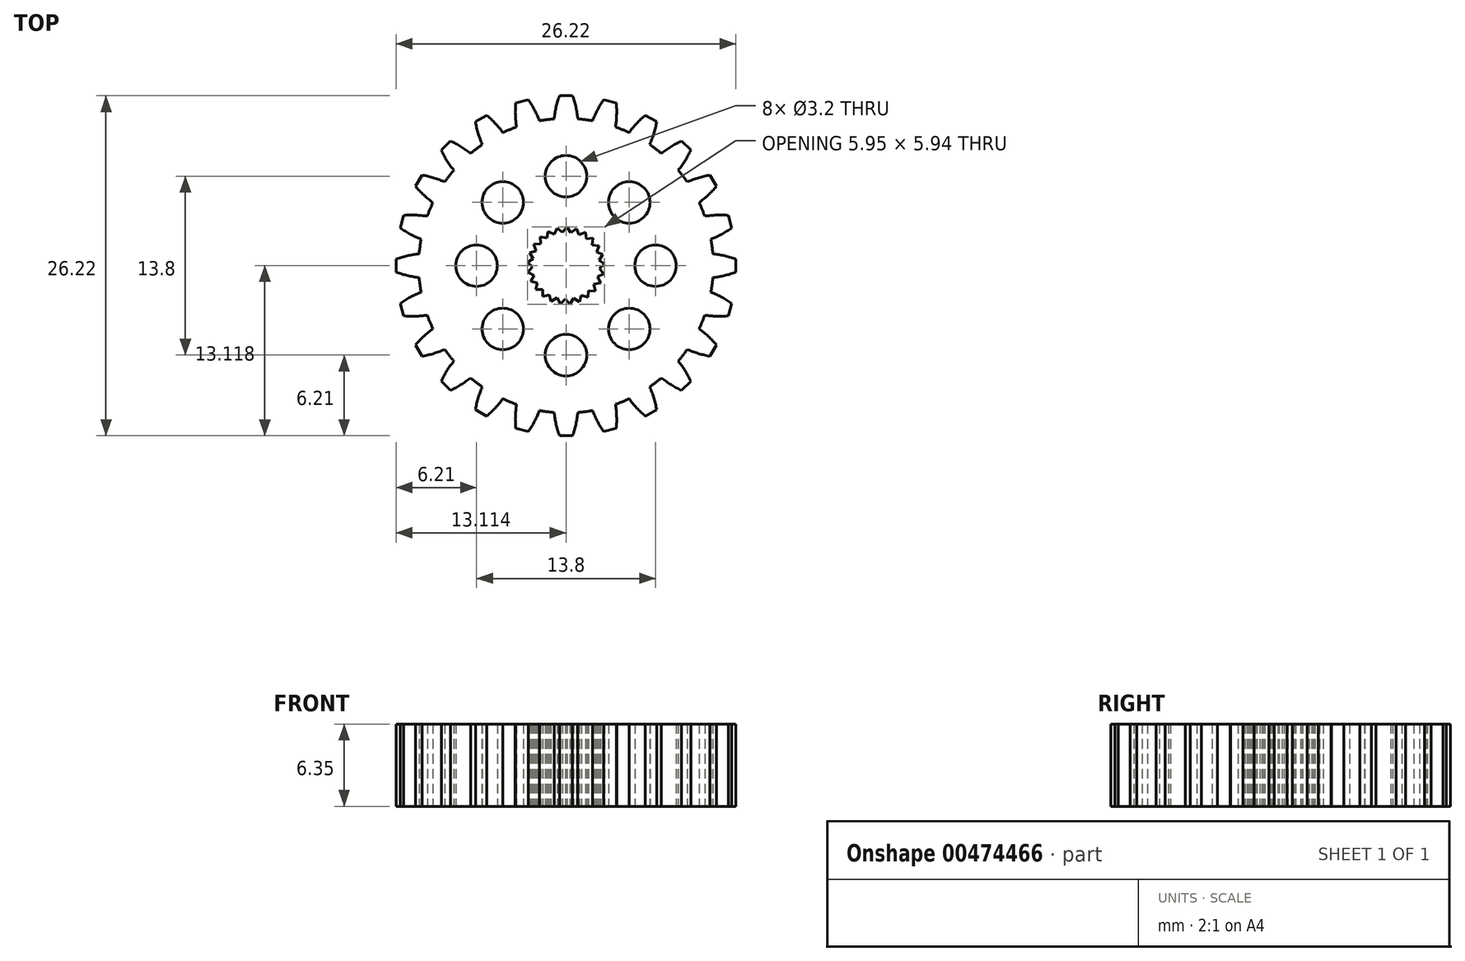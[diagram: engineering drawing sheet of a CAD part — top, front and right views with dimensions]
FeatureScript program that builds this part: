
annotation { "Feature Type Name" : "Feature", "Feature Type Description" : "" }
export const myFeature = defineFeature(function(context is Context, id is Id, definition is map)
    precondition{}
    {
        {
            var Q0;
            Q0=qCreatedBy(makeId("Top.planeOp"),FACE);
            var sketch = newSketch(context, id + "F0", { "sketchPlane" : qUnion([Q0])});
            skLineSegment(sketch, "E0", {"start": v(-0.5, 13.1) * mm, "end": v(0.5, 13.1) * mm});
            skArc(sketch, "E1", {"start": v(-0.5, 13.1) * mm, "mid": v(-0.76, 12.23) * mm, "end": v(-0.91, 11.32) * mm});
            skArc(sketch, "E2.MirrorCS", {"start": v(0.5, 13.1) * mm, "mid": v(0.76, 12.23) * mm, "end": v(0.91, 11.32) * mm});
            skPoint(sketch, "E3.center", {"position": v(0, 0) * mm});
            skLineSegment(sketch, "E4", {"start": v(-2.48, 1.65) * mm, "end": v(-2.31, 1.15) * mm});
            skLineSegment(sketch, "E5", {"start": v(-2.31, 1.15) * mm, "end": v(-2.81, 0.98) * mm});
            skLineSegment(sketch, "E6.1.0", {"start": v(-2.81, 0.98) * mm, "end": v(-2.53, 0.54) * mm});
            skLineSegment(sketch, "E6.1.1", {"start": v(-2.53, 0.54) * mm, "end": v(-2.97, 0.25) * mm});
            skLineSegment(sketch, "E6.2.0", {"start": v(-2.97, 0.25) * mm, "end": v(-2.58, -0.1) * mm});
            skLineSegment(sketch, "E6.2.1", {"start": v(-2.58, -0.1) * mm, "end": v(-2.94, -0.5) * mm});
            skLineSegment(sketch, "E6.3.0", {"start": v(-2.94, -0.5) * mm, "end": v(-2.47, -0.74) * mm});
            skLineSegment(sketch, "E6.3.1", {"start": v(-2.47, -0.74) * mm, "end": v(-2.72, -1.2) * mm});
            skLineSegment(sketch, "E6.4.0", {"start": v(-2.72, -1.2) * mm, "end": v(-2.21, -1.34) * mm});
            skLineSegment(sketch, "E6.4.1", {"start": v(-2.21, -1.34) * mm, "end": v(-2.34, -1.85) * mm});
            skLineSegment(sketch, "E6.5.0", {"start": v(-2.34, -1.85) * mm, "end": v(-1.8, -1.84) * mm});
            skLineSegment(sketch, "E6.5.1", {"start": v(-1.8, -1.84) * mm, "end": v(-1.8, -2.37) * mm});
            skLineSegment(sketch, "E6.6.0", {"start": v(-1.8, -2.37) * mm, "end": v(-1.3, -2.24) * mm});
            skLineSegment(sketch, "E6.6.1", {"start": v(-1.3, -2.24) * mm, "end": v(-1.16, -2.75) * mm});
            skLineSegment(sketch, "E6.7.0", {"start": v(-1.16, -2.75) * mm, "end": v(-0.7, -2.49) * mm});
            skLineSegment(sketch, "E6.7.1", {"start": v(-0.7, -2.49) * mm, "end": v(-0.44, -2.95) * mm});
            skLineSegment(sketch, "E6.8.0", {"start": v(-0.44, -2.95) * mm, "end": v(-0.06, -2.58) * mm});
            skLineSegment(sketch, "E6.8.1", {"start": v(-0.06, -2.58) * mm, "end": v(0.3, -2.96) * mm});
            skLineSegment(sketch, "E6.9.0", {"start": v(0.3, -2.96) * mm, "end": v(0.59, -2.52) * mm});
            skLineSegment(sketch, "E6.9.1", {"start": v(0.59, -2.52) * mm, "end": v(1.04, -2.8) * mm});
            skLineSegment(sketch, "E6.10.0", {"start": v(1.04, -2.8) * mm, "end": v(1.2, -2.3) * mm});
            skLineSegment(sketch, "E6.10.1", {"start": v(1.2, -2.3) * mm, "end": v(1.7, -2.45) * mm});
            skLineSegment(sketch, "E6.11.0", {"start": v(1.7, -2.45) * mm, "end": v(1.73, -1.92) * mm});
            skLineSegment(sketch, "E6.11.1", {"start": v(1.73, -1.92) * mm, "end": v(2.25, -1.95) * mm});
            skLineSegment(sketch, "E6.12.0", {"start": v(2.25, -1.95) * mm, "end": v(2.15, -1.43) * mm});
            skLineSegment(sketch, "E6.12.1", {"start": v(2.15, -1.43) * mm, "end": v(2.67, -1.33) * mm});
            skLineSegment(sketch, "E6.13.0", {"start": v(2.67, -1.33) * mm, "end": v(2.44, -0.85) * mm});
            skLineSegment(sketch, "E6.13.1", {"start": v(2.44, -0.85) * mm, "end": v(2.91, -0.62) * mm});
            skLineSegment(sketch, "E6.14.0", {"start": v(2.91, -0.62) * mm, "end": v(2.57, -0.22) * mm});
            skLineSegment(sketch, "E6.14.1", {"start": v(2.57, -0.22) * mm, "end": v(2.98, 0.12) * mm});
            skLineSegment(sketch, "E6.15.0", {"start": v(2.98, 0.12) * mm, "end": v(2.55, 0.43) * mm});
            skLineSegment(sketch, "E6.15.1", {"start": v(2.55, 0.43) * mm, "end": v(2.85, 0.86) * mm});
            skLineSegment(sketch, "E6.16.0", {"start": v(2.85, 0.86) * mm, "end": v(2.36, 1.05) * mm});
            skLineSegment(sketch, "E6.16.1", {"start": v(2.36, 1.05) * mm, "end": v(2.55, 1.54) * mm});
            skLineSegment(sketch, "E6.17.0", {"start": v(2.55, 1.54) * mm, "end": v(2.03, 1.6) * mm});
            skLineSegment(sketch, "E6.17.1", {"start": v(2.03, 1.6) * mm, "end": v(2.09, 2.13) * mm});
            skLineSegment(sketch, "E6.18.0", {"start": v(2.09, 2.13) * mm, "end": v(1.56, 2.06) * mm});
            skLineSegment(sketch, "E6.18.1", {"start": v(1.56, 2.06) * mm, "end": v(1.5, 2.58) * mm});
            skLineSegment(sketch, "E6.19.0", {"start": v(1.5, 2.58) * mm, "end": v(1, 2.38) * mm});
            skLineSegment(sketch, "E6.19.1", {"start": v(1, 2.38) * mm, "end": v(0.8, 2.87) * mm});
            skLineSegment(sketch, "E6.20.0", {"start": v(0.8, 2.87) * mm, "end": v(0.38, 2.56) * mm});
            skLineSegment(sketch, "E6.20.1", {"start": v(0.38, 2.56) * mm, "end": v(0.07, 2.98) * mm});
            skLineSegment(sketch, "E6.21.0", {"start": v(0.07, 2.98) * mm, "end": v(-0.27, 2.57) * mm});
            skLineSegment(sketch, "E6.21.1", {"start": v(-0.27, 2.57) * mm, "end": v(-0.68, 2.9) * mm});
            skLineSegment(sketch, "E6.22.0", {"start": v(-0.68, 2.9) * mm, "end": v(-0.9, 2.42) * mm});
            skLineSegment(sketch, "E6.22.1", {"start": v(-0.9, 2.42) * mm, "end": v(-1.38, 2.64) * mm});
            skLineSegment(sketch, "E6.23.0", {"start": v(-1.38, 2.64) * mm, "end": v(-1.47, 2.12) * mm});
            skLineSegment(sketch, "E6.23.1", {"start": v(-1.47, 2.12) * mm, "end": v(-2, 2.22) * mm});
            skLineSegment(sketch, "E6.24.0", {"start": v(-2, 2.22) * mm, "end": v(-1.95, 1.69) * mm});
            skLineSegment(sketch, "E6.24.1", {"start": v(-1.95, 1.69) * mm, "end": v(-2.48, 1.65) * mm});
            skCircle(sketch, "E7", {"center": v(0, 6.9) * mm, "radius": 1.6 * mm});
            skCircle(sketch, "E8.1.0", {"center": v(-4.88, 4.88) * mm, "radius": 1.6 * mm});
            skCircle(sketch, "E8.2.0", {"center": v(-6.9, 0) * mm, "radius": 1.6 * mm});
            skCircle(sketch, "E8.3.0", {"center": v(-4.88, -4.88) * mm, "radius": 1.6 * mm});
            skCircle(sketch, "E8.4.0", {"center": v(0, -6.9) * mm, "radius": 1.6 * mm});
            skCircle(sketch, "E8.5.0", {"center": v(4.88, -4.88) * mm, "radius": 1.6 * mm});
            skCircle(sketch, "E8.6.0", {"center": v(6.9, 0) * mm, "radius": 1.6 * mm});
            skCircle(sketch, "E8.7.0", {"center": v(4.88, 4.88) * mm, "radius": 1.6 * mm});
            skPoint(sketch, "E9.1.4", {"position": v(-0.5, 13.1) * mm});
            skArc(sketch, "E10", {"start": v(2.05, 11.18) * mm, "mid": v(1.48, 11.26) * mm, "end": v(0.91, 11.32) * mm});
            skPoint(sketch, "E11.orphan", {"position": v(2.9, 12.8) * mm});
            skPoint(sketch, "E12.orphan", {"position": v(0.94, 11) * mm});
            skPoint(sketch, "E13.orphan", {"position": v(-0.94, 11) * mm});
            skPoint(sketch, "E14.orphan", {"position": v(-2.9, 12.8) * mm});
            skArc(sketch, "E15.1.0", {"start": v(-0.91, 11.32) * mm, "mid": v(-1.48, 11.26) * mm, "end": v(-2.05, 11.18) * mm});
            skPoint(sketch, "E15.1.1", {"position": v(-3.88, 12.53) * mm});
            skArc(sketch, "E15.1.2", {"start": v(-3.88, 12.53) * mm, "mid": v(-3.9, 11.61) * mm, "end": v(-3.81, 10.7) * mm});
            skPoint(sketch, "E15.1.3", {"position": v(-3.75, 10.38) * mm});
            skArc(sketch, "E15.1.5", {"start": v(-2.9, 12.8) * mm, "mid": v(-2.43, 12.01) * mm, "end": v(-2.05, 11.18) * mm});
            skLineSegment(sketch, "E15.1.6", {"start": v(-3.88, 12.53) * mm, "end": v(-2.9, 12.8) * mm});
            skPoint(sketch, "E15.1.7", {"position": v(-1.94, 10.87) * mm});
            skArc(sketch, "E15.2.0", {"start": v(-3.81, 10.7) * mm, "mid": v(-4.35, 10.5) * mm, "end": v(-4.87, 10.26) * mm});
            skPoint(sketch, "E15.2.1", {"position": v(-6.99, 11.1) * mm});
            skArc(sketch, "E15.2.2", {"start": v(-6.99, 11.1) * mm, "mid": v(-6.78, 10.2) * mm, "end": v(-6.45, 9.35) * mm});
            skPoint(sketch, "E15.2.3", {"position": v(-6.31, 9.06) * mm});
            skPoint(sketch, "E15.2.4", {"position": v(-3.88, 12.53) * mm});
            skArc(sketch, "E15.2.5", {"start": v(-6.12, 11.6) * mm, "mid": v(-5.45, 10.97) * mm, "end": v(-4.87, 10.26) * mm});
            skLineSegment(sketch, "E15.2.6", {"start": v(-6.99, 11.1) * mm, "end": v(-6.12, 11.6) * mm});
            skPoint(sketch, "E15.2.7", {"position": v(-4.69, 10) * mm});
            skArc(sketch, "E15.3.0", {"start": v(-6.45, 9.35) * mm, "mid": v(-6.92, 9.01) * mm, "end": v(-7.36, 8.65) * mm});
            skPoint(sketch, "E15.3.1", {"position": v(-9.62, 8.91) * mm});
            skArc(sketch, "E15.3.2", {"start": v(-9.62, 8.91) * mm, "mid": v(-9.19, 8.1) * mm, "end": v(-8.65, 7.36) * mm});
            skPoint(sketch, "E15.3.3", {"position": v(-8.44, 7.11) * mm});
            skPoint(sketch, "E15.3.4", {"position": v(-6.99, 11.1) * mm});
            skArc(sketch, "E15.3.5", {"start": v(-8.91, 9.62) * mm, "mid": v(-8.1, 9.19) * mm, "end": v(-7.36, 8.65) * mm});
            skLineSegment(sketch, "E15.3.6", {"start": v(-9.62, 8.91) * mm, "end": v(-8.91, 9.62) * mm});
            skPoint(sketch, "E15.3.7", {"position": v(-7.11, 8.44) * mm});
            skArc(sketch, "E15.4.0", {"start": v(-8.65, 7.36) * mm, "mid": v(-9.01, 6.92) * mm, "end": v(-9.35, 6.45) * mm});
            skPoint(sketch, "E15.4.1", {"position": v(-11.6, 6.12) * mm});
            skArc(sketch, "E15.4.2", {"start": v(-11.6, 6.12) * mm, "mid": v(-10.97, 5.45) * mm, "end": v(-10.26, 4.87) * mm});
            skPoint(sketch, "E15.4.3", {"position": v(-10, 4.69) * mm});
            skPoint(sketch, "E15.4.4", {"position": v(-9.62, 8.91) * mm});
            skArc(sketch, "E15.4.5", {"start": v(-11.1, 6.99) * mm, "mid": v(-10.2, 6.78) * mm, "end": v(-9.35, 6.45) * mm});
            skLineSegment(sketch, "E15.4.6", {"start": v(-11.6, 6.12) * mm, "end": v(-11.1, 6.99) * mm});
            skPoint(sketch, "E15.4.7", {"position": v(-9.06, 6.31) * mm});
            skArc(sketch, "E15.5.0", {"start": v(-10.26, 4.87) * mm, "mid": v(-10.5, 4.35) * mm, "end": v(-10.7, 3.81) * mm});
            skPoint(sketch, "E15.5.1", {"position": v(-12.8, 2.9) * mm});
            skArc(sketch, "E15.5.2", {"start": v(-12.8, 2.9) * mm, "mid": v(-12.01, 2.43) * mm, "end": v(-11.18, 2.05) * mm});
            skPoint(sketch, "E15.5.3", {"position": v(-10.87, 1.94) * mm});
            skPoint(sketch, "E15.5.4", {"position": v(-11.6, 6.12) * mm});
            skArc(sketch, "E15.5.5", {"start": v(-12.53, 3.88) * mm, "mid": v(-11.61, 3.9) * mm, "end": v(-10.7, 3.81) * mm});
            skLineSegment(sketch, "E15.5.6", {"start": v(-12.8, 2.9) * mm, "end": v(-12.53, 3.88) * mm});
            skPoint(sketch, "E15.5.7", {"position": v(-10.38, 3.75) * mm});
            skArc(sketch, "E15.6.0", {"start": v(-11.18, 2.05) * mm, "mid": v(-11.26, 1.48) * mm, "end": v(-11.32, 0.91) * mm});
            skPoint(sketch, "E15.6.1", {"position": v(-13.1, -0.5) * mm});
            skArc(sketch, "E15.6.2", {"start": v(-13.1, -0.5) * mm, "mid": v(-12.23, -0.76) * mm, "end": v(-11.32, -0.91) * mm});
            skPoint(sketch, "E15.6.3", {"position": v(-11, -0.94) * mm});
            skPoint(sketch, "E15.6.4", {"position": v(-12.8, 2.9) * mm});
            skArc(sketch, "E15.6.5", {"start": v(-13.1, 0.5) * mm, "mid": v(-12.23, 0.76) * mm, "end": v(-11.32, 0.91) * mm});
            skLineSegment(sketch, "E15.6.6", {"start": v(-13.1, -0.5) * mm, "end": v(-13.1, 0.5) * mm});
            skPoint(sketch, "E15.6.7", {"position": v(-11, 0.94) * mm});
            skArc(sketch, "E15.7.0", {"start": v(-11.32, -0.91) * mm, "mid": v(-11.26, -1.48) * mm, "end": v(-11.18, -2.05) * mm});
            skPoint(sketch, "E15.7.1", {"position": v(-12.53, -3.88) * mm});
            skArc(sketch, "E15.7.2", {"start": v(-12.53, -3.88) * mm, "mid": v(-11.61, -3.9) * mm, "end": v(-10.7, -3.81) * mm});
            skPoint(sketch, "E15.7.3", {"position": v(-10.38, -3.75) * mm});
            skPoint(sketch, "E15.7.4", {"position": v(-13.1, -0.5) * mm});
            skArc(sketch, "E15.7.5", {"start": v(-12.8, -2.9) * mm, "mid": v(-12.01, -2.43) * mm, "end": v(-11.18, -2.05) * mm});
            skLineSegment(sketch, "E15.7.6", {"start": v(-12.53, -3.88) * mm, "end": v(-12.8, -2.9) * mm});
            skPoint(sketch, "E15.7.7", {"position": v(-10.87, -1.94) * mm});
            skArc(sketch, "E15.8.0", {"start": v(-10.7, -3.81) * mm, "mid": v(-10.5, -4.35) * mm, "end": v(-10.26, -4.87) * mm});
            skPoint(sketch, "E15.8.1", {"position": v(-11.1, -6.99) * mm});
            skArc(sketch, "E15.8.2", {"start": v(-11.1, -6.99) * mm, "mid": v(-10.2, -6.78) * mm, "end": v(-9.35, -6.45) * mm});
            skPoint(sketch, "E15.8.3", {"position": v(-9.06, -6.31) * mm});
            skPoint(sketch, "E15.8.4", {"position": v(-12.53, -3.88) * mm});
            skArc(sketch, "E15.8.5", {"start": v(-11.6, -6.12) * mm, "mid": v(-10.97, -5.45) * mm, "end": v(-10.26, -4.87) * mm});
            skLineSegment(sketch, "E15.8.6", {"start": v(-11.1, -6.99) * mm, "end": v(-11.6, -6.12) * mm});
            skPoint(sketch, "E15.8.7", {"position": v(-10, -4.69) * mm});
            skArc(sketch, "E15.9.0", {"start": v(-9.35, -6.45) * mm, "mid": v(-9.01, -6.92) * mm, "end": v(-8.65, -7.36) * mm});
            skPoint(sketch, "E15.9.1", {"position": v(-8.91, -9.62) * mm});
            skArc(sketch, "E15.9.2", {"start": v(-8.91, -9.62) * mm, "mid": v(-8.1, -9.19) * mm, "end": v(-7.36, -8.65) * mm});
            skPoint(sketch, "E15.9.3", {"position": v(-7.11, -8.44) * mm});
            skPoint(sketch, "E15.9.4", {"position": v(-11.1, -6.99) * mm});
            skArc(sketch, "E15.9.5", {"start": v(-9.62, -8.91) * mm, "mid": v(-9.19, -8.1) * mm, "end": v(-8.65, -7.36) * mm});
            skLineSegment(sketch, "E15.9.6", {"start": v(-8.91, -9.62) * mm, "end": v(-9.62, -8.91) * mm});
            skPoint(sketch, "E15.9.7", {"position": v(-8.44, -7.11) * mm});
            skArc(sketch, "E15.10.0", {"start": v(-7.36, -8.65) * mm, "mid": v(-6.92, -9.01) * mm, "end": v(-6.45, -9.35) * mm});
            skPoint(sketch, "E15.10.1", {"position": v(-6.12, -11.6) * mm});
            skArc(sketch, "E15.10.2", {"start": v(-6.12, -11.6) * mm, "mid": v(-5.45, -10.97) * mm, "end": v(-4.87, -10.26) * mm});
            skPoint(sketch, "E15.10.3", {"position": v(-4.69, -10) * mm});
            skPoint(sketch, "E15.10.4", {"position": v(-8.91, -9.62) * mm});
            skArc(sketch, "E15.10.5", {"start": v(-6.99, -11.1) * mm, "mid": v(-6.78, -10.2) * mm, "end": v(-6.45, -9.35) * mm});
            skLineSegment(sketch, "E15.10.6", {"start": v(-6.12, -11.6) * mm, "end": v(-6.99, -11.1) * mm});
            skPoint(sketch, "E15.10.7", {"position": v(-6.31, -9.06) * mm});
            skArc(sketch, "E15.11.0", {"start": v(-4.87, -10.26) * mm, "mid": v(-4.35, -10.5) * mm, "end": v(-3.81, -10.7) * mm});
            skPoint(sketch, "E15.11.1", {"position": v(-2.9, -12.8) * mm});
            skArc(sketch, "E15.11.2", {"start": v(-2.9, -12.8) * mm, "mid": v(-2.43, -12.01) * mm, "end": v(-2.05, -11.18) * mm});
            skPoint(sketch, "E15.11.3", {"position": v(-1.94, -10.87) * mm});
            skPoint(sketch, "E15.11.4", {"position": v(-6.12, -11.6) * mm});
            skArc(sketch, "E15.11.5", {"start": v(-3.88, -12.53) * mm, "mid": v(-3.9, -11.61) * mm, "end": v(-3.81, -10.7) * mm});
            skLineSegment(sketch, "E15.11.6", {"start": v(-2.9, -12.8) * mm, "end": v(-3.88, -12.53) * mm});
            skPoint(sketch, "E15.11.7", {"position": v(-3.75, -10.38) * mm});
            skArc(sketch, "E15.12.0", {"start": v(-2.05, -11.18) * mm, "mid": v(-1.48, -11.26) * mm, "end": v(-0.91, -11.32) * mm});
            skPoint(sketch, "E15.12.1", {"position": v(0.5, -13.1) * mm});
            skArc(sketch, "E15.12.2", {"start": v(0.5, -13.1) * mm, "mid": v(0.76, -12.23) * mm, "end": v(0.91, -11.32) * mm});
            skPoint(sketch, "E15.12.3", {"position": v(0.94, -11) * mm});
            skPoint(sketch, "E15.12.4", {"position": v(-2.9, -12.8) * mm});
            skArc(sketch, "E15.12.5", {"start": v(-0.5, -13.1) * mm, "mid": v(-0.76, -12.23) * mm, "end": v(-0.91, -11.32) * mm});
            skLineSegment(sketch, "E15.12.6", {"start": v(0.5, -13.1) * mm, "end": v(-0.5, -13.1) * mm});
            skPoint(sketch, "E15.12.7", {"position": v(-0.94, -11) * mm});
            skArc(sketch, "E15.13.0", {"start": v(0.91, -11.32) * mm, "mid": v(1.48, -11.26) * mm, "end": v(2.05, -11.18) * mm});
            skPoint(sketch, "E15.13.1", {"position": v(3.88, -12.53) * mm});
            skArc(sketch, "E15.13.2", {"start": v(3.88, -12.53) * mm, "mid": v(3.9, -11.61) * mm, "end": v(3.81, -10.7) * mm});
            skPoint(sketch, "E15.13.3", {"position": v(3.75, -10.38) * mm});
            skPoint(sketch, "E15.13.4", {"position": v(0.5, -13.1) * mm});
            skArc(sketch, "E15.13.5", {"start": v(2.9, -12.8) * mm, "mid": v(2.43, -12.01) * mm, "end": v(2.05, -11.18) * mm});
            skLineSegment(sketch, "E15.13.6", {"start": v(3.88, -12.53) * mm, "end": v(2.9, -12.8) * mm});
            skPoint(sketch, "E15.13.7", {"position": v(1.94, -10.87) * mm});
            skArc(sketch, "E15.14.0", {"start": v(3.81, -10.7) * mm, "mid": v(4.35, -10.5) * mm, "end": v(4.87, -10.26) * mm});
            skPoint(sketch, "E15.14.1", {"position": v(6.99, -11.1) * mm});
            skArc(sketch, "E15.14.2", {"start": v(6.99, -11.1) * mm, "mid": v(6.78, -10.2) * mm, "end": v(6.45, -9.35) * mm});
            skPoint(sketch, "E15.14.3", {"position": v(6.31, -9.06) * mm});
            skPoint(sketch, "E15.14.4", {"position": v(3.88, -12.53) * mm});
            skArc(sketch, "E15.14.5", {"start": v(6.12, -11.6) * mm, "mid": v(5.45, -10.97) * mm, "end": v(4.87, -10.26) * mm});
            skLineSegment(sketch, "E15.14.6", {"start": v(6.99, -11.1) * mm, "end": v(6.12, -11.6) * mm});
            skPoint(sketch, "E15.14.7", {"position": v(4.69, -10) * mm});
            skArc(sketch, "E15.15.0", {"start": v(6.45, -9.35) * mm, "mid": v(6.92, -9.01) * mm, "end": v(7.36, -8.65) * mm});
            skPoint(sketch, "E15.15.1", {"position": v(9.62, -8.91) * mm});
            skArc(sketch, "E15.15.2", {"start": v(9.62, -8.91) * mm, "mid": v(9.19, -8.1) * mm, "end": v(8.65, -7.36) * mm});
            skPoint(sketch, "E15.15.3", {"position": v(8.44, -7.11) * mm});
            skPoint(sketch, "E15.15.4", {"position": v(6.99, -11.1) * mm});
            skArc(sketch, "E15.15.5", {"start": v(8.91, -9.62) * mm, "mid": v(8.1, -9.19) * mm, "end": v(7.36, -8.65) * mm});
            skLineSegment(sketch, "E15.15.6", {"start": v(9.62, -8.91) * mm, "end": v(8.91, -9.62) * mm});
            skPoint(sketch, "E15.15.7", {"position": v(7.11, -8.44) * mm});
            skArc(sketch, "E15.16.0", {"start": v(8.65, -7.36) * mm, "mid": v(9.01, -6.92) * mm, "end": v(9.35, -6.45) * mm});
            skPoint(sketch, "E15.16.1", {"position": v(11.6, -6.12) * mm});
            skArc(sketch, "E15.16.2", {"start": v(11.6, -6.12) * mm, "mid": v(10.97, -5.45) * mm, "end": v(10.26, -4.87) * mm});
            skPoint(sketch, "E15.16.3", {"position": v(10, -4.69) * mm});
            skPoint(sketch, "E15.16.4", {"position": v(9.62, -8.91) * mm});
            skArc(sketch, "E15.16.5", {"start": v(11.1, -6.99) * mm, "mid": v(10.2, -6.78) * mm, "end": v(9.35, -6.45) * mm});
            skLineSegment(sketch, "E15.16.6", {"start": v(11.6, -6.12) * mm, "end": v(11.1, -6.99) * mm});
            skPoint(sketch, "E15.16.7", {"position": v(9.06, -6.31) * mm});
            skArc(sketch, "E15.17.0", {"start": v(10.26, -4.87) * mm, "mid": v(10.5, -4.35) * mm, "end": v(10.7, -3.81) * mm});
            skPoint(sketch, "E15.17.1", {"position": v(12.8, -2.9) * mm});
            skArc(sketch, "E15.17.2", {"start": v(12.8, -2.9) * mm, "mid": v(12.01, -2.43) * mm, "end": v(11.18, -2.05) * mm});
            skPoint(sketch, "E15.17.3", {"position": v(10.87, -1.94) * mm});
            skPoint(sketch, "E15.17.4", {"position": v(11.6, -6.12) * mm});
            skArc(sketch, "E15.17.5", {"start": v(12.53, -3.88) * mm, "mid": v(11.61, -3.9) * mm, "end": v(10.7, -3.81) * mm});
            skLineSegment(sketch, "E15.17.6", {"start": v(12.8, -2.9) * mm, "end": v(12.53, -3.88) * mm});
            skPoint(sketch, "E15.17.7", {"position": v(10.38, -3.75) * mm});
            skArc(sketch, "E15.18.0", {"start": v(11.18, -2.05) * mm, "mid": v(11.26, -1.48) * mm, "end": v(11.32, -0.91) * mm});
            skPoint(sketch, "E15.18.1", {"position": v(13.1, 0.5) * mm});
            skArc(sketch, "E15.18.2", {"start": v(13.1, 0.5) * mm, "mid": v(12.23, 0.76) * mm, "end": v(11.32, 0.91) * mm});
            skPoint(sketch, "E15.18.3", {"position": v(11, 0.94) * mm});
            skPoint(sketch, "E15.18.4", {"position": v(12.8, -2.9) * mm});
            skArc(sketch, "E15.18.5", {"start": v(13.1, -0.5) * mm, "mid": v(12.23, -0.76) * mm, "end": v(11.32, -0.91) * mm});
            skLineSegment(sketch, "E15.18.6", {"start": v(13.1, 0.5) * mm, "end": v(13.1, -0.5) * mm});
            skPoint(sketch, "E15.18.7", {"position": v(11, -0.94) * mm});
            skArc(sketch, "E15.19.0", {"start": v(11.32, 0.91) * mm, "mid": v(11.26, 1.48) * mm, "end": v(11.18, 2.05) * mm});
            skPoint(sketch, "E15.19.1", {"position": v(12.53, 3.88) * mm});
            skArc(sketch, "E15.19.2", {"start": v(12.53, 3.88) * mm, "mid": v(11.61, 3.9) * mm, "end": v(10.7, 3.81) * mm});
            skPoint(sketch, "E15.19.3", {"position": v(10.38, 3.75) * mm});
            skPoint(sketch, "E15.19.4", {"position": v(13.1, 0.5) * mm});
            skArc(sketch, "E15.19.5", {"start": v(12.8, 2.9) * mm, "mid": v(12.01, 2.43) * mm, "end": v(11.18, 2.05) * mm});
            skLineSegment(sketch, "E15.19.6", {"start": v(12.53, 3.88) * mm, "end": v(12.8, 2.9) * mm});
            skPoint(sketch, "E15.19.7", {"position": v(10.87, 1.94) * mm});
            skArc(sketch, "E15.20.0", {"start": v(10.7, 3.81) * mm, "mid": v(10.5, 4.35) * mm, "end": v(10.26, 4.87) * mm});
            skPoint(sketch, "E15.20.1", {"position": v(11.1, 6.99) * mm});
            skArc(sketch, "E15.20.2", {"start": v(11.1, 6.99) * mm, "mid": v(10.2, 6.78) * mm, "end": v(9.35, 6.45) * mm});
            skPoint(sketch, "E15.20.3", {"position": v(9.06, 6.31) * mm});
            skPoint(sketch, "E15.20.4", {"position": v(12.53, 3.88) * mm});
            skArc(sketch, "E15.20.5", {"start": v(11.6, 6.12) * mm, "mid": v(10.97, 5.45) * mm, "end": v(10.26, 4.87) * mm});
            skLineSegment(sketch, "E15.20.6", {"start": v(11.1, 6.99) * mm, "end": v(11.6, 6.12) * mm});
            skPoint(sketch, "E15.20.7", {"position": v(10, 4.69) * mm});
            skArc(sketch, "E15.21.0", {"start": v(9.35, 6.45) * mm, "mid": v(9.01, 6.92) * mm, "end": v(8.65, 7.36) * mm});
            skPoint(sketch, "E15.21.1", {"position": v(8.91, 9.62) * mm});
            skArc(sketch, "E15.21.2", {"start": v(8.91, 9.62) * mm, "mid": v(8.1, 9.19) * mm, "end": v(7.36, 8.65) * mm});
            skPoint(sketch, "E15.21.3", {"position": v(7.11, 8.44) * mm});
            skPoint(sketch, "E15.21.4", {"position": v(11.1, 6.99) * mm});
            skArc(sketch, "E15.21.5", {"start": v(9.62, 8.91) * mm, "mid": v(9.19, 8.1) * mm, "end": v(8.65, 7.36) * mm});
            skLineSegment(sketch, "E15.21.6", {"start": v(8.91, 9.62) * mm, "end": v(9.62, 8.91) * mm});
            skPoint(sketch, "E15.21.7", {"position": v(8.44, 7.11) * mm});
            skArc(sketch, "E15.22.0", {"start": v(7.36, 8.65) * mm, "mid": v(6.92, 9.01) * mm, "end": v(6.45, 9.35) * mm});
            skPoint(sketch, "E15.22.1", {"position": v(6.12, 11.6) * mm});
            skArc(sketch, "E15.22.2", {"start": v(6.12, 11.6) * mm, "mid": v(5.45, 10.97) * mm, "end": v(4.87, 10.26) * mm});
            skPoint(sketch, "E15.22.3", {"position": v(4.69, 10) * mm});
            skPoint(sketch, "E15.22.4", {"position": v(8.91, 9.62) * mm});
            skArc(sketch, "E15.22.5", {"start": v(6.99, 11.1) * mm, "mid": v(6.78, 10.2) * mm, "end": v(6.45, 9.35) * mm});
            skLineSegment(sketch, "E15.22.6", {"start": v(6.12, 11.6) * mm, "end": v(6.99, 11.1) * mm});
            skPoint(sketch, "E15.22.7", {"position": v(6.31, 9.06) * mm});
            skArc(sketch, "E15.23.0", {"start": v(4.87, 10.26) * mm, "mid": v(4.35, 10.5) * mm, "end": v(3.81, 10.7) * mm});
            skArc(sketch, "E15.23.2", {"start": v(2.9, 12.8) * mm, "mid": v(2.43, 12.01) * mm, "end": v(2.05, 11.18) * mm});
            skPoint(sketch, "E15.23.3", {"position": v(1.94, 10.87) * mm});
            skPoint(sketch, "E15.23.4", {"position": v(6.12, 11.6) * mm});
            skArc(sketch, "E15.23.5", {"start": v(3.88, 12.53) * mm, "mid": v(3.9, 11.61) * mm, "end": v(3.81, 10.7) * mm});
            skLineSegment(sketch, "E15.23.6", {"start": v(2.9, 12.8) * mm, "end": v(3.88, 12.53) * mm});
            skPoint(sketch, "E15.23.7", {"position": v(3.75, 10.38) * mm});
            skSolve(sketch);
        }
        {
            var Q0;
            Q0=qSketchRegion(id+"F0",true);
            extrude(context, id + "F1", {"entities" : qUnion([Q0]), "depth" : 6.35 * mm});
        }
    });
